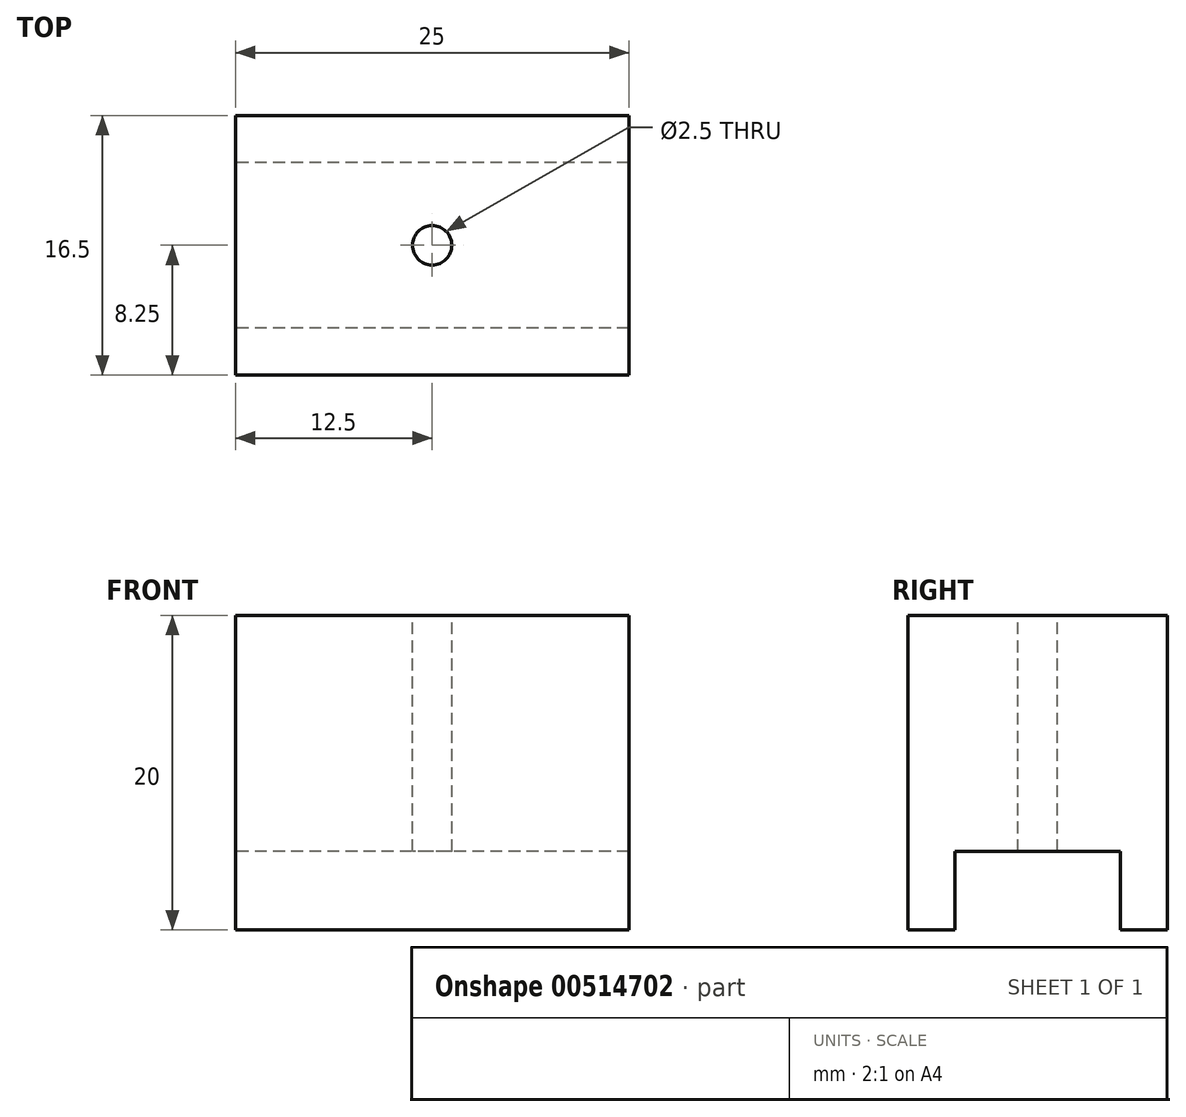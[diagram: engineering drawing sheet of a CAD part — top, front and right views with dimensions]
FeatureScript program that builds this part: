
annotation { "Feature Type Name" : "Feature", "Feature Type Description" : "" }
export const myFeature = defineFeature(function(context is Context, id is Id, definition is map)
    precondition{}
    {
        {
            var Q0;
            Q0=qCreatedBy(makeId("Top.planeOp"),FACE);
            var sketch = newSketch(context, id + "F0", { "sketchPlane" : qUnion([Q0])});
            skLineSegment(sketch, "E0.bottom", {"start": v(12.5, -8.25) * mm, "end": v(-12.5, -8.25) * mm});
            skLineSegment(sketch, "E0.top", {"start": v(12.5, 8.25) * mm, "end": v(-12.5, 8.25) * mm});
            skLineSegment(sketch, "E0.left", {"start": v(12.5, -8.25) * mm, "end": v(12.5, 8.25) * mm});
            skLineSegment(sketch, "E0.right", {"start": v(-12.5, -8.25) * mm, "end": v(-12.5, 8.25) * mm});
            skPoint(sketch, "E0.middle", {"position": v(0, 0) * mm});
            skLineSegment(sketch, "E1.bottom", {"start": v(12.5, -5.25) * mm, "end": v(-12.5, -5.25) * mm});
            skLineSegment(sketch, "E1.top", {"start": v(12.5, 5.25) * mm, "end": v(-12.5, 5.25) * mm});
            skLineSegment(sketch, "E1.left", {"start": v(12.5, -5.25) * mm, "end": v(12.5, 5.25) * mm});
            skLineSegment(sketch, "E1.right", {"start": v(-12.5, -5.25) * mm, "end": v(-12.5, 5.25) * mm});
            skSolve(sketch);
        }
        {
            var Q0;
            {var subQ0=sQuery(id+"F0.wireOp",EDGE,"E0.top");Q0=makeQuery(id+"F0.imprint","IMPRINT",FACE,{"disambiguationData":[TD([[makeQuery(id+"F0.imprint","IMPRINT",EDGE,{"derivedFrom":subQ0}),1.0]])]});}
            var Q1;
            Q1=makeQuery(id+"F0.imprint","IMPRINT",FACE,{"disambiguationData":[TD([[makeQuery(id+"F0.imprint","IMPRINT",EDGE,{"derivedFrom":sQuery(id+"F0.wireOp",EDGE,"E1.bottom")}),-1.0]])]});
            var Q2;
            {var subQ0=sQuery(id+"F0.wireOp",EDGE,"E0.bottom");Q2=makeQuery(id+"F0.imprint","IMPRINT",FACE,{"disambiguationData":[TD([[makeQuery(id+"F0.imprint","IMPRINT",EDGE,{"derivedFrom":subQ0}),-1.0]])]});}
            extrude(context, id + "F1", {"entities" : qUnion([Q0, Q1, Q2]), "depth" : 20 * mm, "offsetDistance" : 25 * mm});
        }
        {
            var Q0;
            Q0=makeQuery(id+"F0.imprint","IMPRINT",FACE,{"disambiguationData":[TD([[makeQuery(id+"F0.imprint","IMPRINT",EDGE,{"derivedFrom":sQuery(id+"F0.wireOp",EDGE,"E1.bottom")}),-1.0]])]});
            extrude(context, id + "F2", {"entities" : qUnion([Q0]), "operationType" : NewBodyOperationType.REMOVE, "depth" : 5 * mm, "offsetDistance" : 25 * mm});
        }
        {
            var Q0;
            Q0=makeQuery(id+"F1.opExtrude","CAP_FACE",FACE,{"disambiguationData":[OSD([sQuery(id+"F0.wireOp",EDGE,"E0.bottom"),sQuery(id+"F0.wireOp",EDGE,"E0.top"),sQuery(id+"F0.wireOp",EDGE,"E0.left"),sQuery(id+"F0.wireOp",EDGE,"E0.right"),sQuery(id+"F0.wireOp",EDGE,"E1.left"),sQuery(id+"F0.wireOp",EDGE,"E1.right")])],"isStart":false});
            var sketch = newSketch(context, id + "F3", { "sketchPlane" : qUnion([Q0])});
            skCircle(sketch, "E2", {"center": v(0, 0) * mm, "radius": 1.25 * mm});
            skSolve(sketch);
        }
        {
            var Q0;
            Q0=makeQuery(id+"F3.imprint","IMPRINT",FACE,{"disambiguationData":[TD([[makeQuery(id+"F3.imprint","IMPRINT",EDGE,{"derivedFrom":sQuery(id+"F3.wireOp",EDGE,"E2")}),1.0]])]});
            extrude(context, id + "F4", {"entities" : qUnion([Q0]), "operationType" : NewBodyOperationType.REMOVE, "endBound" : BoundingType.THROUGH_ALL, "oppositeDirection" : true, "depth" : 25 * mm, "offsetDistance" : 25 * mm});
        }
    });
